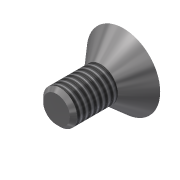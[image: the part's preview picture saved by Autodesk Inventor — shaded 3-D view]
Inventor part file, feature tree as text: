
AUTODESK INVENTOR PART (.ipt)
format: ipt  version: 2013 (Build 170138000, 138)  size: 107,008 bytes
history: native  units: in
note: dims shown in document units (in); Inventor stores cm internally (conversion verified against a paired STEP export)
features: sketch x2, revolve x1, thread x1, chamfer x1, extrude x1
ambient origin geometry x8: Origin, YZ Plane, XZ Plane, XY Plane, X Axis, Y Axis, Z Axis, Center Point
bodies: Solid1 (feature_tree)
feature tree (6):
  revolve  "Revolution1"  [1 undecoded]
  thread  "Thread1"  [1 undecoded]
  chamfer  "Chamfer1"  Distance=0.2054in
  extrude  "Extrusion1"  TaperAngle=90.0deg  [1 undecoded]
  sketch  "Sketch1"  dims[d0=0.19in d2=0.375in d3=0.2817in]
  sketch  "Sketch2"  dims[d4=0.127in d5=0.2054in d6=90.0deg d7=1.0in d8=0.0in d9=0.02in d10=0.125in d11=45.0deg d12=0.125in d13=0.08in d14=0.0in]
note: 3 required parameter values undecoded (feature->parameter linkage not recoverable at this tier; creation-order binding heuristic only, values carry confidence <= 0.55)